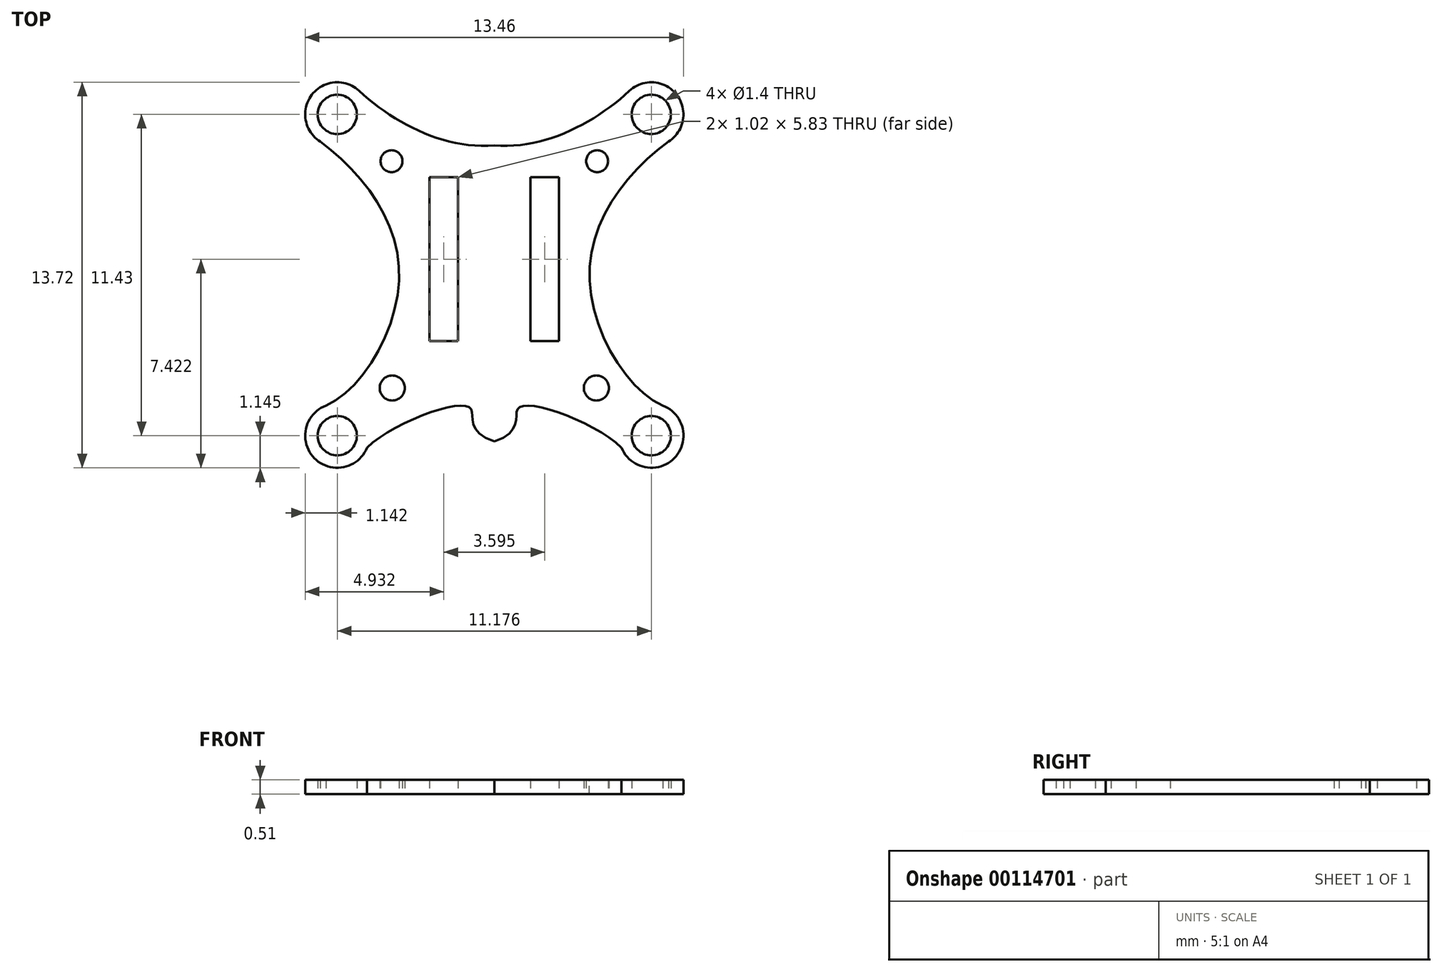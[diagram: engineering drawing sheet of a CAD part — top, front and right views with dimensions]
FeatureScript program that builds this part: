
annotation { "Feature Type Name" : "Feature", "Feature Type Description" : "" }
export const myFeature = defineFeature(function(context is Context, id is Id, definition is map)
    precondition{}
    {
        {
            var Q0;
            Q0=qCreatedBy(makeId("Top.planeOp"),FACE);
            var sketch = newSketch(context, id + "F0", { "sketchPlane" : qUnion([Q0])});
            skLineSegment(sketch, "E0.bottom", {"start": v(-6.73, -6.86) * mm, "end": v(6.73, -6.86) * mm, "construction": true});
            skLineSegment(sketch, "E0.top", {"start": v(-6.73, 6.86) * mm, "end": v(6.73, 6.86) * mm, "construction": true});
            skLineSegment(sketch, "E0.left", {"start": v(-6.73, -6.86) * mm, "end": v(-6.73, 6.86) * mm, "construction": true});
            skLineSegment(sketch, "E0.right", {"start": v(6.73, -6.86) * mm, "end": v(6.73, 6.86) * mm, "construction": true});
            skPoint(sketch, "E0.middle", {"position": v(0, 0) * mm});
            skLineSegment(sketch, "E1", {"start": v(0, 6.86) * mm, "end": v(0, -6.86) * mm, "construction": true});
            skCircle(sketch, "E2", {"center": v(-5.59, 5.72) * mm, "radius": 0.7 * mm});
            skCircle(sketch, "E3", {"center": v(-3.66, 4.05) * mm, "radius": 0.4 * mm});
            skLineSegment(sketch, "E4.bottom", {"start": v(-2.3, 3.48) * mm, "end": v(-1.3, 3.48) * mm});
            skLineSegment(sketch, "E4.top", {"start": v(-2.3, -2.35) * mm, "end": v(-1.3, -2.35) * mm});
            skLineSegment(sketch, "E4.left", {"start": v(-2.3, 3.48) * mm, "end": v(-2.3, -2.35) * mm});
            skLineSegment(sketch, "E4.right", {"start": v(-1.3, 3.48) * mm, "end": v(-1.3, -2.35) * mm});
            skCircle(sketch, "E5", {"center": v(-5.59, -5.72) * mm, "radius": 0.7 * mm});
            skCircle(sketch, "E6", {"center": v(-3.63, -4.02) * mm, "radius": 0.45 * mm});
            skArc(sketch, "E7", {"start": v(-4.8, 6.55) * mm, "mid": v(-6.5, 6.41) * mm, "end": v(-6.2, 4.75) * mm});
            skArc(sketch, "E8", {"start": v(-6, -4.65) * mm, "mid": v(-6.4, -6.51) * mm, "end": v(-4.53, -6.14) * mm});
            skFitSpline(sketch, "E9", {"points": [v(-6.2, 4.75) * mm, v(-3.39, 0) * mm, v(-6, -4.65) * mm], "startDerivative": vector(8.92, -6.55) * mm, "endDerivative": vector(-8, -3.52) * mm});
            skLineSegment(sketch, "E10", {"start": v(-6.73, 0) * mm, "end": v(6.73, 0) * mm, "construction": true});
            skLineSegment(sketch, "E11.MirrorCS", {"start": v(1.3, 3.48) * mm, "end": v(1.3, -2.35) * mm});
            skLineSegment(sketch, "E12.MirrorCS", {"start": v(2.3, 3.48) * mm, "end": v(1.3, 3.48) * mm});
            skLineSegment(sketch, "E13.MirrorCS", {"start": v(2.3, 3.48) * mm, "end": v(2.3, -2.35) * mm});
            skLineSegment(sketch, "E14.MirrorCS", {"start": v(2.3, -2.35) * mm, "end": v(1.3, -2.35) * mm});
            skCircle(sketch, "E15.MirrorC", {"center": v(3.66, 4.05) * mm, "radius": 0.4 * mm});
            skCircle(sketch, "E16.MirrorC", {"center": v(3.63, -4.02) * mm, "radius": 0.45 * mm});
            skFitSpline(sketch, "E17.MirrorCS", {"points": [v(6.2, 4.75) * mm, v(3.39, 0) * mm, v(6, -4.65) * mm], "startDerivative": vector(-8.92, -6.55) * mm, "endDerivative": vector(8, -3.52) * mm});
            skArc(sketch, "E18.MirrorC", {"start": v(4.8, 6.55) * mm, "mid": v(6.5, 6.41) * mm, "end": v(6.2, 4.75) * mm});
            skCircle(sketch, "E19.MirrorC", {"center": v(5.59, 5.72) * mm, "radius": 0.7 * mm});
            skArc(sketch, "E20.MirrorC", {"start": v(6, -4.65) * mm, "mid": v(6.4, -6.51) * mm, "end": v(4.53, -6.14) * mm});
            skCircle(sketch, "E21.MirrorC", {"center": v(5.59, -5.72) * mm, "radius": 0.7 * mm});
            skFitSpline(sketch, "E22", {"points": [v(-4.8, 6.55) * mm, v(0, 4.61) * mm], "startDerivative": vector(3.77, -3.47) * mm, "endDerivative": vector(5.33, 0.45) * mm});
            skFitSpline(sketch, "E23", {"points": [v(-4.53, -6.14) * mm, v(-0.88, -4.7) * mm, v(0, -5.92) * mm], "startDerivative": vector(4.27, 4.27) * mm, "endDerivative": vector(8.65, -2.97) * mm});
            skFitSpline(sketch, "E24.MirrorCS", {"points": [v(4.53, -6.14) * mm, v(0.88, -4.7) * mm, v(0, -5.92) * mm], "startDerivative": vector(-4.27, 4.27) * mm, "endDerivative": vector(-8.65, -2.97) * mm});
            skFitSpline(sketch, "E25.MirrorCS", {"points": [v(4.8, 6.55) * mm, v(0, 4.61) * mm], "startDerivative": vector(-3.77, -3.47) * mm, "endDerivative": vector(-5.33, 0.45) * mm});
            skSolve(sketch);
        }
        {
            var Q0;
            Q0 = qSketchRegion(id + "F0", true);
            var Q1;
            Q1 = qConstructionFilter(qBodyType(qCreatedBy(id + "F0" ,EDGE), BodyType.WIRE), ConstructionObject.NO);
            extrude(context, id + "F1", {"entities" : qUnion([Q0]), "surfaceEntities" : qUnion([Q1]), "depth" : 0.5 * mm});
        }
    });
